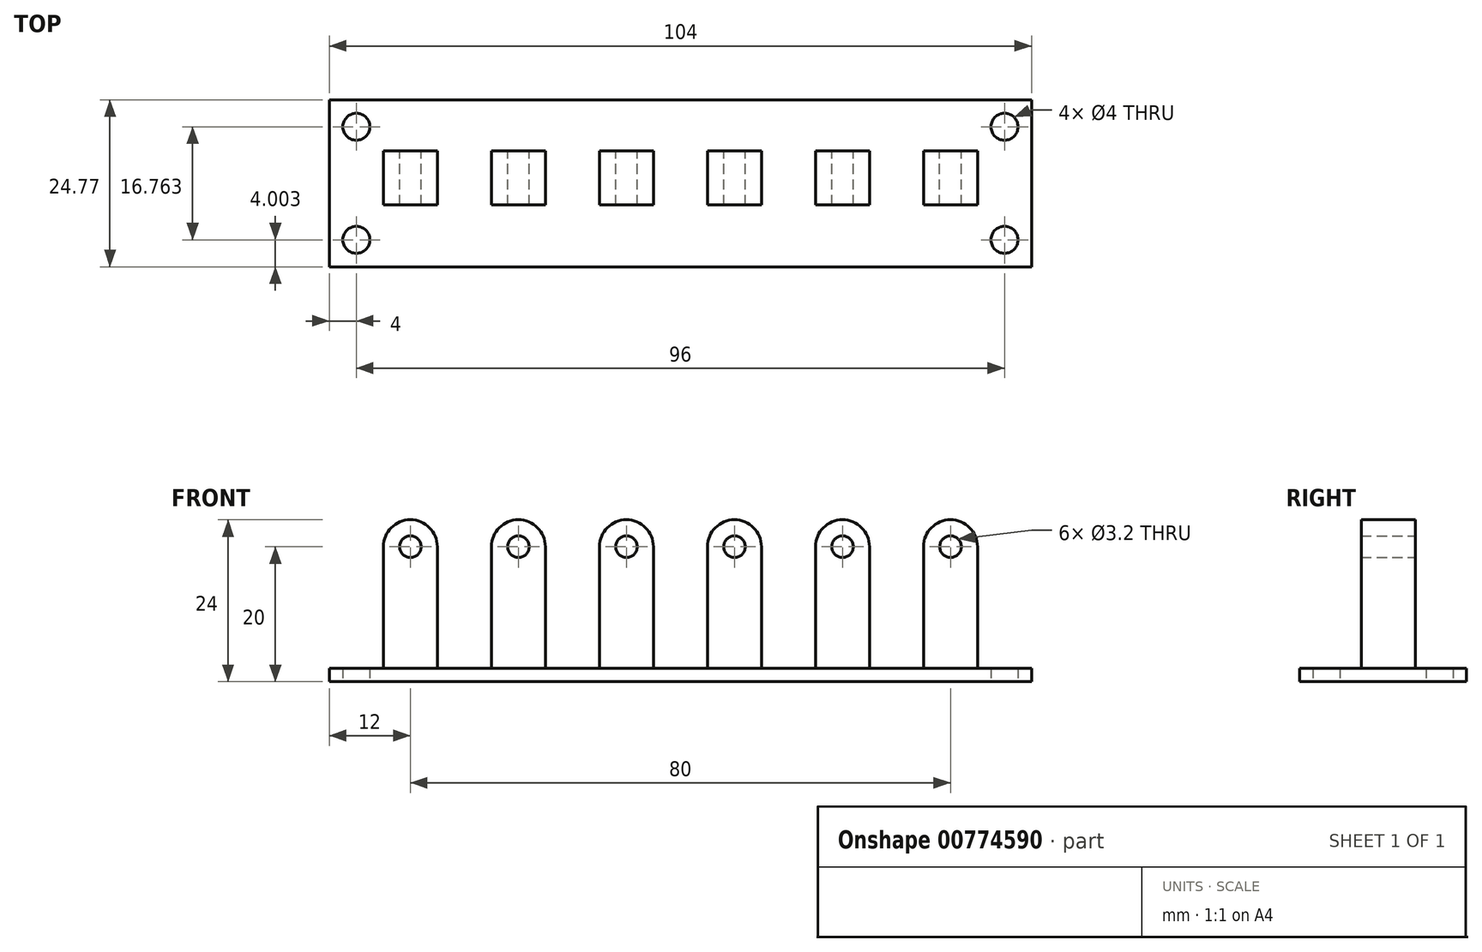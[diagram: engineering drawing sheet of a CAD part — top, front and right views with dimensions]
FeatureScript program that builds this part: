
annotation { "Feature Type Name" : "Feature", "Feature Type Description" : "" }
export const myFeature = defineFeature(function(context is Context, id is Id, definition is map)
    precondition{}
    {
        {
            var Q0;
            Q0=qCreatedBy(makeId("Top.planeOp"),FACE);
            var sketch = newSketch(context, id + "F0", { "sketchPlane" : qUnion([Q0])});
            skLineSegment(sketch, "E0.bottom", {"start": v(-52, 11.6) * mm, "end": v(52, 11.6) * mm});
            skLineSegment(sketch, "E0.top", {"start": v(-52, -13.16) * mm, "end": v(52, -13.16) * mm});
            skLineSegment(sketch, "E0.left", {"start": v(-52, 11.6) * mm, "end": v(-52, -13.16) * mm});
            skLineSegment(sketch, "E0.right", {"start": v(52, 11.6) * mm, "end": v(52, -13.16) * mm});
            skCircle(sketch, "E1", {"center": v(-48, 7.6) * mm, "radius": 2 * mm});
            skCircle(sketch, "E2", {"center": v(-48, -9.16) * mm, "radius": 2 * mm});
            skCircle(sketch, "E3", {"center": v(48, -9.16) * mm, "radius": 2 * mm});
            skCircle(sketch, "E4", {"center": v(48, 7.6) * mm, "radius": 2 * mm});
            skSolve(sketch);
        }
        {
            var Q0;
            Q0 = qSketchRegion(id + "F0", true);
            extrude(context, id + "F1", {"entities" : qUnion([Q0]), "depth" : 2 * mm, "offsetDistance" : 25.4 * mm});
        }
        {
            var Q0;
            Q0=qCreatedBy(makeId("Front.planeOp"),FACE);
            var sketch = newSketch(context, id + "F2", { "sketchPlane" : qUnion([Q0])});
            skLineSegment(sketch, "E5.bottom", {"start": v(-44, 0) * mm, "end": v(-36, 0) * mm});
            skLineSegment(sketch, "E5.top", {"start": v(-44, 20) * mm, "end": v(-36, 20) * mm, "construction": true});
            skLineSegment(sketch, "E5.left", {"start": v(-44, 0) * mm, "end": v(-44, 20) * mm});
            skLineSegment(sketch, "E5.right", {"start": v(-36, 0) * mm, "end": v(-36, 20) * mm});
            skCircle(sketch, "E6", {"center": v(-40, 20) * mm, "radius": 4 * mm});
            skCircle(sketch, "E7", {"center": v(-40, 20) * mm, "radius": 1.6 * mm});
            skLineSegment(sketch, "E8.bottom", {"start": v(-28, 0) * mm, "end": v(-20, 0) * mm});
            skLineSegment(sketch, "E8.top", {"start": v(-28, 20) * mm, "end": v(-20, 20) * mm, "construction": true});
            skLineSegment(sketch, "E8.left", {"start": v(-28, 0) * mm, "end": v(-28, 20) * mm});
            skLineSegment(sketch, "E8.right", {"start": v(-20, 0) * mm, "end": v(-20, 20) * mm});
            skCircle(sketch, "E9", {"center": v(-24, 20) * mm, "radius": 4 * mm});
            skCircle(sketch, "E10", {"center": v(-24, 20) * mm, "radius": 1.6 * mm});
            skLineSegment(sketch, "E11.bottom", {"start": v(-12, 0) * mm, "end": v(-4, 0) * mm});
            skLineSegment(sketch, "E11.top", {"start": v(-12, 20) * mm, "end": v(-4, 20) * mm, "construction": true});
            skLineSegment(sketch, "E11.left", {"start": v(-12, 0) * mm, "end": v(-12, 20) * mm});
            skLineSegment(sketch, "E11.right", {"start": v(-4, 0) * mm, "end": v(-4, 20) * mm});
            skCircle(sketch, "E12", {"center": v(-8, 20) * mm, "radius": 4 * mm});
            skCircle(sketch, "E13", {"center": v(-8, 20) * mm, "radius": 1.6 * mm});
            skLineSegment(sketch, "E14.bottom", {"start": v(4, 0) * mm, "end": v(12, 0) * mm});
            skLineSegment(sketch, "E14.top", {"start": v(4, 20) * mm, "end": v(12, 20) * mm, "construction": true});
            skLineSegment(sketch, "E14.left", {"start": v(4, 0) * mm, "end": v(4, 20) * mm});
            skLineSegment(sketch, "E14.right", {"start": v(12, 0) * mm, "end": v(12, 20) * mm});
            skCircle(sketch, "E15", {"center": v(8, 20) * mm, "radius": 4 * mm});
            skCircle(sketch, "E16", {"center": v(8, 20) * mm, "radius": 1.6 * mm});
            skLineSegment(sketch, "E17.bottom", {"start": v(20, 0) * mm, "end": v(28, 0) * mm});
            skLineSegment(sketch, "E17.top", {"start": v(20, 20) * mm, "end": v(28, 20) * mm, "construction": true});
            skLineSegment(sketch, "E17.left", {"start": v(20, 0) * mm, "end": v(20, 20) * mm});
            skLineSegment(sketch, "E17.right", {"start": v(28, 0) * mm, "end": v(28, 20) * mm});
            skCircle(sketch, "E18", {"center": v(24, 20) * mm, "radius": 4 * mm});
            skCircle(sketch, "E19", {"center": v(24, 20) * mm, "radius": 1.6 * mm});
            skLineSegment(sketch, "E20.bottom", {"start": v(36, 0) * mm, "end": v(44, 0) * mm});
            skLineSegment(sketch, "E20.top", {"start": v(36, 20) * mm, "end": v(44, 20) * mm, "construction": true});
            skLineSegment(sketch, "E20.left", {"start": v(36, 0) * mm, "end": v(36, 20) * mm});
            skLineSegment(sketch, "E20.right", {"start": v(44, 0) * mm, "end": v(44, 20) * mm});
            skCircle(sketch, "E21", {"center": v(40, 20) * mm, "radius": 4 * mm});
            skCircle(sketch, "E22", {"center": v(40, 20) * mm, "radius": 1.6 * mm});
            skSolve(sketch);
        }
        {
            var Q0;
            Q0=makeQuery(id+"F2.imprint","IMPRINT",FACE,{"disambiguationData":[TD([[makeQuery(id+"F2.imprint","IMPRINT",EDGE,{"derivedFrom":sQuery(id+"F2.wireOp",EDGE,"E8.bottom")}),1.0]])]});
            var Q1;
            Q1=makeQuery(id+"F2.imprint","IMPRINT",FACE,{"disambiguationData":[TD([[makeQuery(id+"F2.imprint","IMPRINT",EDGE,{"derivedFrom":sQuery(id+"F2.wireOp",EDGE,"E10")}),-1.0]])]});
            var Q2;
            Q2=makeQuery(id+"F2.imprint","IMPRINT",FACE,{"disambiguationData":[TD([[makeQuery(id+"F2.imprint","IMPRINT",EDGE,{"derivedFrom":sQuery(id+"F2.wireOp",EDGE,"E17.bottom")}),1.0]])]});
            var Q3;
            Q3=makeQuery(id+"F2.imprint","IMPRINT",FACE,{"disambiguationData":[TD([[makeQuery(id+"F2.imprint","IMPRINT",EDGE,{"derivedFrom":sQuery(id+"F2.wireOp",EDGE,"E19")}),-1.0]])]});
            var Q4;
            Q4=makeQuery(id+"F2.imprint","IMPRINT",FACE,{"disambiguationData":[TD([[makeQuery(id+"F2.imprint","IMPRINT",EDGE,{"derivedFrom":sQuery(id+"F2.wireOp",EDGE,"E5.bottom")}),1.0]])]});
            var Q5;
            Q5=makeQuery(id+"F2.imprint","IMPRINT",FACE,{"disambiguationData":[TD([[makeQuery(id+"F2.imprint","IMPRINT",EDGE,{"derivedFrom":sQuery(id+"F2.wireOp",EDGE,"E7")}),-1.0]])]});
            var Q6;
            Q6=makeQuery(id+"F2.imprint","IMPRINT",FACE,{"disambiguationData":[TD([[makeQuery(id+"F2.imprint","IMPRINT",EDGE,{"derivedFrom":sQuery(id+"F2.wireOp",EDGE,"E11.bottom")}),1.0]])]});
            var Q7;
            Q7=makeQuery(id+"F2.imprint","IMPRINT",FACE,{"disambiguationData":[TD([[makeQuery(id+"F2.imprint","IMPRINT",EDGE,{"derivedFrom":sQuery(id+"F2.wireOp",EDGE,"E13")}),-1.0]])]});
            var Q8;
            Q8=makeQuery(id+"F2.imprint","IMPRINT",FACE,{"disambiguationData":[TD([[makeQuery(id+"F2.imprint","IMPRINT",EDGE,{"derivedFrom":sQuery(id+"F2.wireOp",EDGE,"E14.bottom")}),1.0]])]});
            var Q9;
            Q9=makeQuery(id+"F2.imprint","IMPRINT",FACE,{"disambiguationData":[TD([[makeQuery(id+"F2.imprint","IMPRINT",EDGE,{"derivedFrom":sQuery(id+"F2.wireOp",EDGE,"E16")}),-1.0]])]});
            var Q10;
            Q10=makeQuery(id+"F2.imprint","IMPRINT",FACE,{"disambiguationData":[TD([[makeQuery(id+"F2.imprint","IMPRINT",EDGE,{"derivedFrom":sQuery(id+"F2.wireOp",EDGE,"E20.bottom")}),1.0]])]});
            var Q11;
            Q11=makeQuery(id+"F2.imprint","IMPRINT",FACE,{"disambiguationData":[TD([[makeQuery(id+"F2.imprint","IMPRINT",EDGE,{"derivedFrom":sQuery(id+"F2.wireOp",EDGE,"E22")}),-1.0]])]});
            extrude(context, id + "F3", {"entities" : qUnion([Q0, Q1, Q2, Q3, Q4, Q5, Q6, Q7, Q8, Q9, Q10, Q11]), "operationType" : NewBodyOperationType.ADD, "endBound" : BoundingType.SYMMETRIC, "depth" : 8 * mm, "offsetDistance" : 25.4 * mm});
        }
    });
